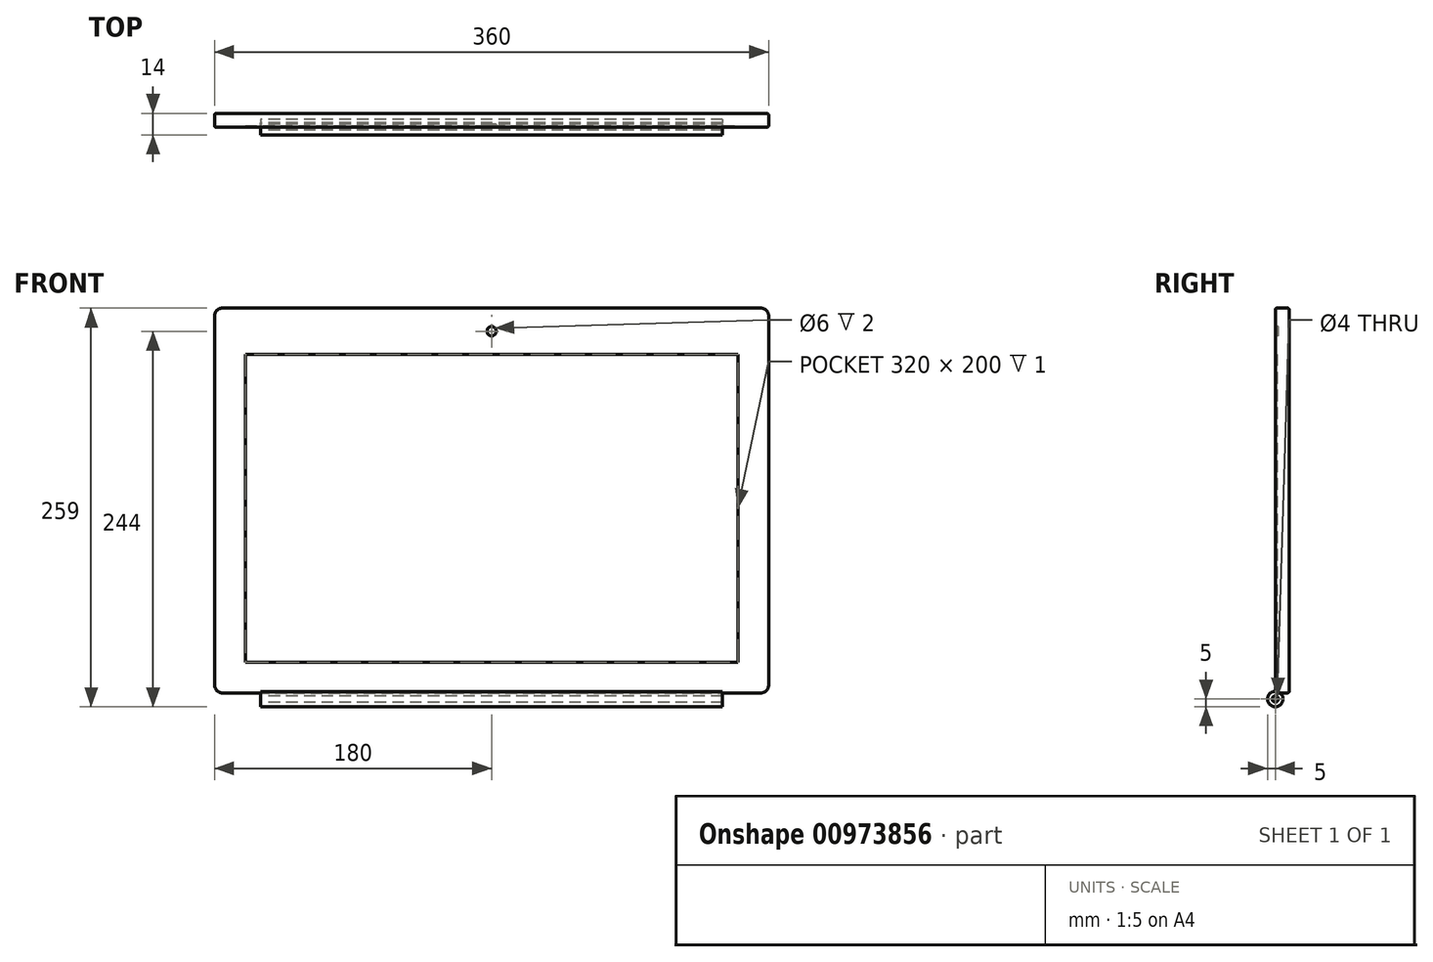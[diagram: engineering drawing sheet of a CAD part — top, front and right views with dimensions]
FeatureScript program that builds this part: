
annotation { "Feature Type Name" : "Feature", "Feature Type Description" : "" }
export const myFeature = defineFeature(function(context is Context, id is Id, definition is map)
    precondition{}
    {
        {
            var Q0;
            Q0=qCreatedBy(makeId("Front.planeOp"),FACE);
            var sketch = newSketch(context, id + "F0", { "sketchPlane" : qUnion([Q0])});
            skLineSegment(sketch, "E0.bottom", {"start": v(-180, 250) * mm, "end": v(180, 250) * mm});
            skLineSegment(sketch, "E0.top", {"start": v(-180, 0) * mm, "end": v(180, 0) * mm});
            skLineSegment(sketch, "E0.left", {"start": v(-180, 250) * mm, "end": v(-180, 0) * mm});
            skLineSegment(sketch, "E0.right", {"start": v(180, 250) * mm, "end": v(180, 0) * mm});
            skSolve(sketch);
        }
        {
            var Q0;
            Q0=makeQuery(id+"F0.imprint","IMPRINT",FACE,{"disambiguationData":[TD([[makeQuery(id+"F0.imprint","IMPRINT",EDGE,{"derivedFrom":sQuery(id+"F0.wireOp",EDGE,"E0.bottom")}),-1.0]])]});
            extrude(context, id + "F1", {"entities" : qUnion([Q0]), "depth" : 9 * mm, "offsetDistance" : 25 * mm});
        }
        {
            var Q0;
            Q0=makeQuery(id+"F1.opExtrude","CAP_FACE",FACE,{"disambiguationData":[OSD([sQuery(id+"F0.wireOp",EDGE,"E0.bottom"),sQuery(id+"F0.wireOp",EDGE,"E0.top"),sQuery(id+"F0.wireOp",EDGE,"E0.left"),sQuery(id+"F0.wireOp",EDGE,"E0.right")])],"isStart":false});
            var sketch = newSketch(context, id + "F2", { "sketchPlane" : qUnion([Q0])});
            skLineSegment(sketch, "E1.bottom", {"start": v(-160, 220) * mm, "end": v(160, 220) * mm});
            skLineSegment(sketch, "E1.top", {"start": v(-160, 20) * mm, "end": v(160, 20) * mm});
            skLineSegment(sketch, "E1.left", {"start": v(-160, 220) * mm, "end": v(-160, 20) * mm});
            skLineSegment(sketch, "E1.right", {"start": v(160, 220) * mm, "end": v(160, 20) * mm});
            skLineSegment(sketch, "E2", {"start": v(0, 20) * mm, "end": v(0, 0) * mm, "construction": true});
            skSolve(sketch);
        }
        {
            var Q0;
            Q0 = qSketchRegion(id + "F2", true);
            extrude(context, id + "F3", {"entities" : qUnion([Q0]), "operationType" : NewBodyOperationType.REMOVE, "oppositeDirection" : true, "depth" : 1 * mm, "offsetDistance" : 25 * mm});
        }
        {
            var Q0;
            Q0=makeQuery(id+"F1.opExtrude","CAP_FACE",FACE,{"disambiguationData":[OSD([sQuery(id+"F0.wireOp",EDGE,"E0.bottom"),sQuery(id+"F0.wireOp",EDGE,"E0.top"),sQuery(id+"F0.wireOp",EDGE,"E0.left"),sQuery(id+"F0.wireOp",EDGE,"E0.right")])],"isStart":false});
            var sketch = newSketch(context, id + "F4", { "sketchPlane" : qUnion([Q0])});
            skCircle(sketch, "E3", {"center": v(0, 235) * mm, "radius": 3 * mm});
            skLineSegment(sketch, "E4", {"start": v(0, 250) * mm, "end": v(0, 235) * mm, "construction": true});
            skLineSegment(sketch, "E5", {"start": v(0, 235) * mm, "end": v(0, 220) * mm, "construction": true});
            skLineSegment(sketch, "E6", {"start": v(0, 220) * mm, "end": v(0, 0) * mm, "construction": true});
            skSolve(sketch);
        }
        {
            var Q0;
            Q0 = qSketchRegion(id + "F4", true);
            extrude(context, id + "F5", {"entities" : qUnion([Q0]), "operationType" : NewBodyOperationType.REMOVE, "oppositeDirection" : true, "depth" : 2 * mm, "offsetDistance" : 25 * mm});
        }
        {
            var Q0;
            Q0=qCreatedBy(makeId("Right.planeOp"),FACE);
            var sketch = newSketch(context, id + "F6", { "sketchPlane" : qUnion([Q0])});
            skCircle(sketch, "E7", {"center": v(-9, -4) * mm, "radius": 5 * mm});
            skCircle(sketch, "E8", {"center": v(-9, -4) * mm, "radius": 2 * mm});
            skLineSegment(sketch, "E9", {"start": v(-9, -4) * mm, "end": v(-9, 0) * mm, "construction": true});
            skSolve(sketch);
        }
        {
            var Q0;
            Q0 = qSketchRegion(id + "F6", true);
            extrude(context, id + "F7", {"entities" : qUnion([Q0]), "operationType" : NewBodyOperationType.ADD, "endBound" : BoundingType.SYMMETRIC, "depth" : 300 * mm, "offsetDistance" : 25 * mm});
        }
        {
            var Q0;
            Q0=makeQuery(id+"F1.opExtrude","SWEPT_EDGE",EDGE,{"disambiguationData":[OSD([sQuery(id+"F0.wireOp",EDGE,"E0.top"),sQuery(id+"F0.wireOp",EDGE,"E0.right")])]});
            var Q1;
            Q1=makeQuery(id+"F1.opExtrude","SWEPT_EDGE",EDGE,{"disambiguationData":[OSD([sQuery(id+"F0.wireOp",EDGE,"E0.bottom"),sQuery(id+"F0.wireOp",EDGE,"E0.right")])]});
            var Q2;
            Q2=makeQuery(id+"F1.opExtrude","SWEPT_EDGE",EDGE,{"disambiguationData":[OSD([sQuery(id+"F0.wireOp",EDGE,"E0.bottom"),sQuery(id+"F0.wireOp",EDGE,"E0.left")])]});
            var Q3;
            Q3=makeQuery(id+"F1.opExtrude","SWEPT_EDGE",EDGE,{"disambiguationData":[OSD([sQuery(id+"F0.wireOp",EDGE,"E0.top"),sQuery(id+"F0.wireOp",EDGE,"E0.left")])]});
            fillet(context, id + "F8", {"entities" : qUnion([Q0, Q1, Q2, Q3]), "radius" : 5 * mm, "tangentPropagation" : true, "allowEdgeOverflow" : false});
        }
        {
            var Q0;
            Q0=makeQuery(id+"F1.opExtrude","CAP_EDGE",EDGE,{"disambiguationData":[OSD([sQuery(id+"F0.wireOp",EDGE,"E0.left")])],"isStart":false});
            var Q1;
            Q1=makeQuery(id+"F1.opExtrude","CAP_EDGE",EDGE,{"disambiguationData":[OSD([sQuery(id+"F0.wireOp",EDGE,"E0.left")])],"isStart":true});
            fillet(context, id + "F9", {"entities" : qUnion([Q0, Q1]), "radius" : 1 * mm, "tangentPropagation" : true, "allowEdgeOverflow" : false});
        }
    });
